# Revit family: Site_Accessories-Bike_Ovella-Systems-Oy_Junior_V-3-Teline_1
name_source: partatom
category: Specialty Equipment
units: mm (PartAtom-declared; Revit-internal decimal feet)

## family parameters
Always vertical = Yes
Cut with Voids When Loaded = No
Enable Cutting in Views = Yes
Maintain Annotation Orientation = No
OmniClass Number = 23.11.29.11.11
OmniClass Title = Bicycle Racks
Part Type = Normal
Room Calculation Point = No
Round Connector Dimension = Use Diameter
Shared = No
Work Plane-Based = No

## types (1)
- Junior - V-3 Teline
    Default Elevation = 0 mm  [stored 0 ft]
    Height = 600 mm  [stored 1.9685 ft]
    Length = 1945 mm  [stored 6.38123 ft]
    Manufacturer = Ovella Systems Oy
    Model = Junior - V-3 Teline
    Product Material = Ovella Systems Oy - Metal - Steel - Black
    Product Page URL = https://www.ovella.fi
    URL = https://www.ovella.fi
    Version = 1
    Width = 320 mm  [stored 1.04987 ft]

note: [stored X ft] marks values corroborated as IEEE doubles in the binary element streams (Revit-internal decimal feet)

## geometry (parser evidence)
native form markers: Sweep x7
no freeform markers — native parametric forms only
